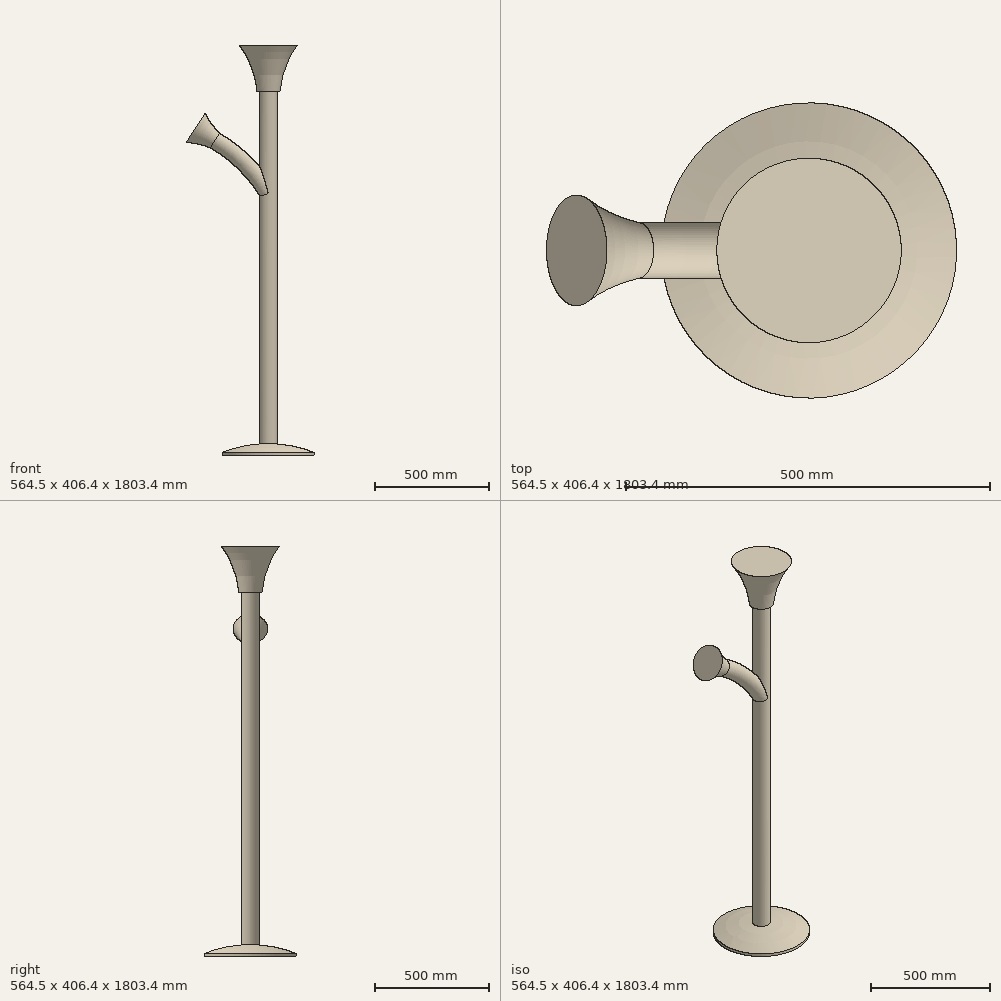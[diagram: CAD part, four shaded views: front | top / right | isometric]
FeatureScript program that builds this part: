
annotation { "Feature Type Name" : "Feature", "Feature Type Description" : "" }
export const myFeature = defineFeature(function(context is Context, id is Id, definition is map)
    precondition{}
    {
        {
            var Q0;
            Q0=qCreatedBy(makeId("Front.planeOp"),FACE);
            var sketch = newSketch(context, id + "F0", { "sketchPlane" : qUnion([Q0])});
            skLineSegment(sketch, "E0", {"start": v(0, 0) * mm, "end": v(0, 1803.4) * mm});
            skLineSegment(sketch, "E1", {"start": v(0, 1803.4) * mm, "end": v(-127, 1803.4) * mm});
            skLineSegment(sketch, "E2", {"start": v(0, 0) * mm, "end": v(-203.2, 0) * mm});
            skLineSegment(sketch, "E3", {"start": v(-203.2, 0) * mm, "end": v(-203.2, 12.7) * mm});
            skArc(sketch, "E4", {"start": v(-203.2, 12.7) * mm, "mid": v(-103.5, 42.19) * mm, "end": v(0, 52.14) * mm});
            skLineSegment(sketch, "E5", {"start": v(-38.1, 50.8) * mm, "end": v(-38.1, 1600.2) * mm});
            skArc(sketch, "E6", {"start": v(-127, 1803.4) * mm, "mid": v(-75.2, 1706.94) * mm, "end": v(-50.8, 1600.2) * mm});
            skLineSegment(sketch, "E7", {"start": v(-50.8, 1600.2) * mm, "end": v(-38.1, 1600.2) * mm});
            skSolve(sketch);
        }
        {
            var Q0;
            {var subQ4=sQuery(id+"F0.wireOp",EDGE,"E1");Q0=makeQuery(id+"F0.imprint","IMPRINT",FACE,{"disambiguationData":[TD([[makeQuery(id+"F0.imprint","IMPRINT",EDGE,{"derivedFrom":subQ4}),1.0]])]});}
            var Q1;
            {var subQ3=sQuery(id+"F0.wireOp",EDGE,"E2");Q1=makeQuery(id+"F0.imprint","IMPRINT",FACE,{"disambiguationData":[TD([[makeQuery(id+"F0.imprint","IMPRINT",EDGE,{"derivedFrom":subQ3}),-1.0]])]});}
            var Q2;
            Q2=sQuery(id+"F0.wireOp",EDGE,"E0");
            revolve(context, id + "F1", {"entities" : qUnion([Q0, Q1]), "axis" : qUnion([Q2]), "revolveType" : RevolveType.FULL});
        }
        {
            var Q0;
            Q0=qCreatedBy(makeId("Front.planeOp"),FACE);
            var sketch = newSketch(context, id + "F2", { "sketchPlane" : qUnion([Q0])});
            skLineSegment(sketch, "E8", {"start": v(0, 0) * mm, "end": v(0, 1066.8) * mm});
            skArc(sketch, "E9", {"start": v(0, 1066.8) * mm, "mid": v(-104.62, 1230.44) * mm, "end": v(-255.4, 1352.86) * mm});
            skArc(sketch, "E10.0", {"start": v(81.47, 1068.71) * mm, "mid": v(-36.34, 1268.04) * mm, "end": v(-213.78, 1416.8) * mm});
            skLineSegment(sketch, "E11", {"start": v(0, 1066.8) * mm, "end": v(0, 1221.23) * mm});
            skLineSegment(sketch, "E12", {"start": v(-213.78, 1416.8) * mm, "end": v(-255.4, 1352.86) * mm});
            skLineSegment(sketch, "E13", {"start": v(-234.6, 1384.83) * mm, "end": v(-319.74, 1440.26) * mm});
            skLineSegment(sketch, "E14", {"start": v(-361.31, 1376.4) * mm, "end": v(-319.74, 1440.26) * mm});
            skArc(sketch, "E15", {"start": v(-255.4, 1352.86) * mm, "mid": v(-307.3, 1369.38) * mm, "end": v(-361.31, 1376.4) * mm});
            skSolve(sketch);
        }
        {
            var Q0;
            {var subQ5=sQuery(id+"F2.wireOp",EDGE,"E9");Q0=makeQuery(id+"F2.imprint","IMPRINT",FACE,{"disambiguationData":[TD([[makeQuery(id+"F2.imprint","IMPRINT",EDGE,{"derivedFrom":subQ5}),-1.0]])]});}
            extrude(context, id + "F3", {"entities" : qUnion([Q0]), "operationType" : NewBodyOperationType.ADD, "depth" : 76.2 * mm, "symmetric" : true});
        }
        {
            var Q0;
            Q0=makeQuery(id+"F3.opExtrude","CAP_EDGE",EDGE,{"disambiguationData":[OSD([sQuery(id+"F2.wireOp",EDGE,"E10.0")])],"isStart":false});
            var Q1;
            Q1=makeQuery(id+"F3.opExtrude","CAP_EDGE",EDGE,{"disambiguationData":[OSD([sQuery(id+"F2.wireOp",EDGE,"E9")])],"isStart":false});
            var Q2;
            Q2=makeQuery(id+"F3.opExtrude","CAP_EDGE",EDGE,{"disambiguationData":[OSD([sQuery(id+"F2.wireOp",EDGE,"E10.0")])],"isStart":true});
            var Q3;
            Q3=makeQuery(id+"F3.opExtrude","CAP_EDGE",EDGE,{"disambiguationData":[OSD([sQuery(id+"F2.wireOp",EDGE,"E9")])],"isStart":true});
            fillet(context, id + "F4", {"entities" : qUnion([Q0, Q1, Q2, Q3]), "radius" : 38.1 * mm, "tangentPropagation" : true, "allowEdgeOverflow" : false});
        }
        {
            var Q0;
            {var subQ2=sQuery(id+"F2.wireOp",EDGE,"E13");Q0=makeQuery(id+"F2.imprint","IMPRINT",FACE,{"disambiguationData":[TD([[makeQuery(id+"F2.imprint","IMPRINT",EDGE,{"derivedFrom":subQ2}),1.0]])]});}
            var Q1;
            Q1=sQuery(id+"F2.wireOp",EDGE,"E13");
            revolve(context, id + "F5", {"operationType" : NewBodyOperationType.ADD, "entities" : qUnion([Q0]), "axis" : qUnion([Q1]), "revolveType" : RevolveType.FULL});
        }
    });
